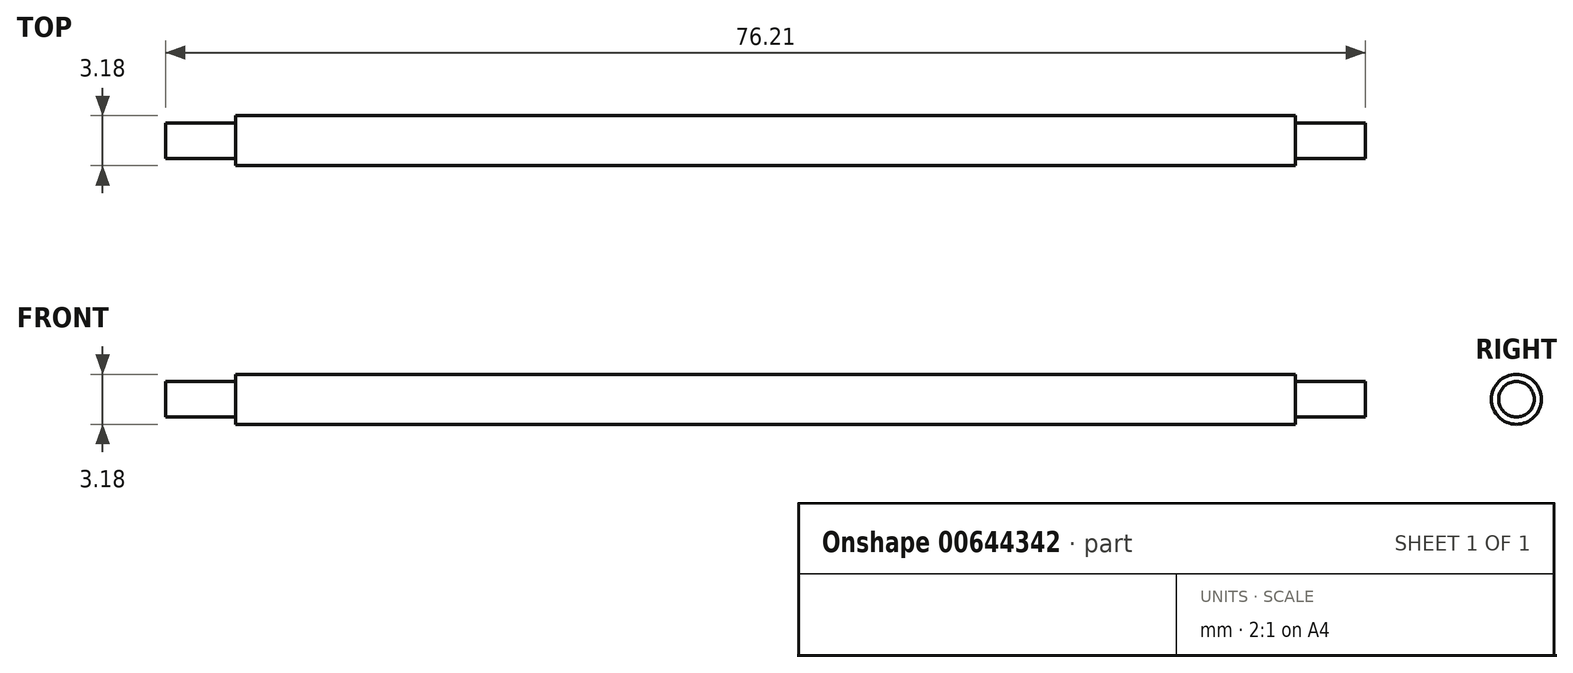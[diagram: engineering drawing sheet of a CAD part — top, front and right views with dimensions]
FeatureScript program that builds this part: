
annotation { "Feature Type Name" : "Feature", "Feature Type Description" : "" }
export const myFeature = defineFeature(function(context is Context, id is Id, definition is map)
    precondition{}
    {
        {
            var Q0;
            Q0=qCreatedBy(makeId("Top.planeOp"),FACE);
            var sketch = newSketch(context, id + "F0", { "sketchPlane" : qUnion([Q0])});
            skLineSegment(sketch, "E0.bottom", {"start": v(0, 0) * mm, "end": v(67.31, 0) * mm});
            skLineSegment(sketch, "E0.top", {"start": v(0, 1.59) * mm, "end": v(67.31, 1.59) * mm});
            skLineSegment(sketch, "E0.left", {"start": v(0, 0) * mm, "end": v(0, 1.59) * mm});
            skLineSegment(sketch, "E0.right", {"start": v(67.31, 0) * mm, "end": v(67.31, 1.59) * mm});
            skPoint(sketch, "E1.oppositeSnap0", {"position": v(0, 0.8) * mm});
            skLineSegment(sketch, "E1.bottom", {"start": v(0, 0) * mm, "end": v(-4.45, 0) * mm});
            skLineSegment(sketch, "E1.top", {"start": v(0, 1.13) * mm, "end": v(-4.45, 1.13) * mm});
            skLineSegment(sketch, "E1.left", {"start": v(0, 0) * mm, "end": v(0, 1.13) * mm});
            skLineSegment(sketch, "E1.right", {"start": v(-4.45, 0) * mm, "end": v(-4.45, 1.13) * mm});
            skLineSegment(sketch, "E2.bottom", {"start": v(67.31, 0) * mm, "end": v(71.76, 0) * mm});
            skLineSegment(sketch, "E2.top", {"start": v(67.31, 1.13) * mm, "end": v(71.76, 1.13) * mm});
            skLineSegment(sketch, "E2.left", {"start": v(67.31, 0) * mm, "end": v(67.31, 1.13) * mm});
            skLineSegment(sketch, "E2.right", {"start": v(71.76, 0) * mm, "end": v(71.76, 1.13) * mm});
            skSolve(sketch);
        }
        {
            var Q0;
            Q0=makeQuery(id+"F0.imprint","IMPRINT",FACE,{"disambiguationData":[TD([[makeQuery(id+"F0.imprint","IMPRINT",EDGE,{"derivedFrom":sQuery(id+"F0.wireOp",EDGE,"E2.bottom")}),1.0]])]});
            var Q1;
            Q1=makeQuery(id+"F0.imprint","IMPRINT",FACE,{"disambiguationData":[TD([[makeQuery(id+"F0.imprint","IMPRINT",EDGE,{"derivedFrom":sQuery(id+"F0.wireOp",EDGE,"E1.bottom")}),-1.0]])]});
            var Q2;
            Q2=makeQuery(id+"F0.imprint","IMPRINT",FACE,{"disambiguationData":[TD([[makeQuery(id+"F0.imprint","IMPRINT",EDGE,{"derivedFrom":sQuery(id+"F0.wireOp",EDGE,"E0.bottom")}),1.0]])]});
            var Q3;
            Q3=sQuery(id+"F0.wireOp",EDGE,"E0.bottom");
            revolve(context, id + "F1", {"entities" : qUnion([Q0, Q1, Q2]), "axis" : qUnion([Q3]), "revolveType" : RevolveType.FULL});
        }
    });
